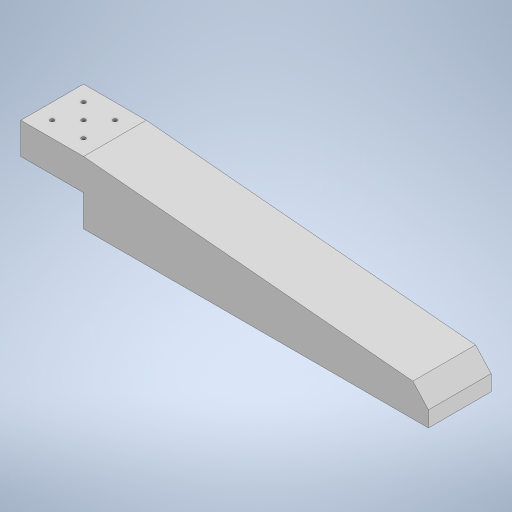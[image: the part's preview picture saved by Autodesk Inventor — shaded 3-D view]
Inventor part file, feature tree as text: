
AUTODESK INVENTOR PART (.ipt)
format: ipt  version: 2023 (Build 270158000, 158)  size: 244,224 bytes
history: native  units: in
note: dims shown in document units (in); Inventor stores cm internally (conversion verified against a paired STEP export)
features: extrude x2, sketch x2, chamfer x1
ambient origin geometry x8: Origin, YZ Plane, XZ Plane, XY Plane, X Axis, Y Axis, Z Axis, Center Point
bodies: Solid1 (feature_tree)
feature tree (5):
  extrude  "Extrusion1"  Depth=26.0in
  chamfer  "Chamfer1"  Distance=2.0in
  extrude  "Extrusion2"  Depth=4.0in TaperAngle=0.0deg
  sketch  "Sketch1"  dims[d0=26.0in d1=8.0in]
  sketch  "Sketch2"  dims[d2=4.0in d3=2.0in d4=4.0in d5=0.0in d6=1.0in d7=0.125in d8=45.0deg d9=0.25in d10=0.25in d11=0.25in d12=0.25in d13=0.25in d14=1.0in d15=1.0in d16=1.0in d17=1.0in d18=1.0in d19=1.0in d20=1.0in d21=1.0in d22=2.0in d23=2.0in d24=4.0in d25=0.0in]
